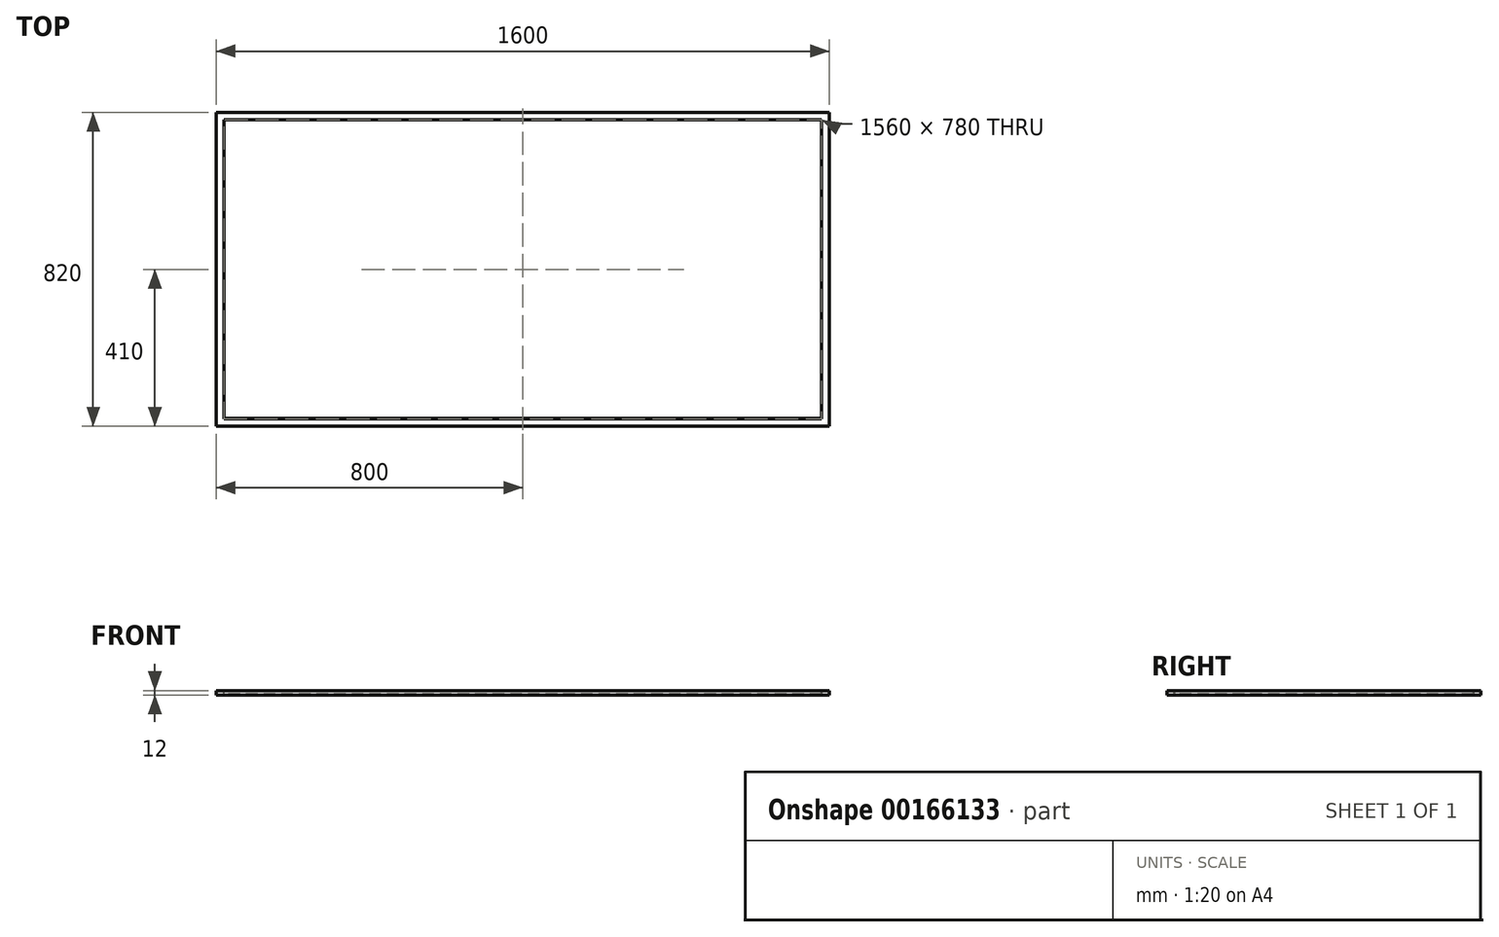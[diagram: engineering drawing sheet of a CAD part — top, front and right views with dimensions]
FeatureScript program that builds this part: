
annotation { "Feature Type Name" : "Feature", "Feature Type Description" : "" }
export const myFeature = defineFeature(function(context is Context, id is Id, definition is map)
    precondition{}
    {
        {
            var Q0;
            Q0=qCreatedBy(makeId("Front.planeOp"),FACE);
            var sketch = newSketch(context, id + "F0", { "sketchPlane" : qUnion([Q0])});
            skLineSegment(sketch, "E0.bottom", {"start": v(0, 0) * mm, "end": v(20, 0) * mm});
            skLineSegment(sketch, "E0.top", {"start": v(0, 12) * mm, "end": v(20, 12) * mm});
            skLineSegment(sketch, "E0.left", {"start": v(0, 0) * mm, "end": v(0, 12) * mm});
            skLineSegment(sketch, "E0.right", {"start": v(20, 0) * mm, "end": v(20, 12) * mm});
            skSolve(sketch);
        }
        {
            var Q0;
            Q0=qCreatedBy(makeId("Top.planeOp"),FACE);
            var sketch = newSketch(context, id + "F1", { "sketchPlane" : qUnion([Q0])});
            skLineSegment(sketch, "E1.bottom", {"start": v(0, 0) * mm, "end": v(1600, 0) * mm});
            skLineSegment(sketch, "E1.top", {"start": v(0, 820) * mm, "end": v(1600, 820) * mm});
            skLineSegment(sketch, "E1.left", {"start": v(0, 0) * mm, "end": v(0, 820) * mm});
            skLineSegment(sketch, "E1.right", {"start": v(1600, 0) * mm, "end": v(1600, 820) * mm});
            skSolve(sketch);
        }
        {
            var Q0;
            Q0=makeQuery(id+"F0.imprint","IMPRINT",FACE,{"disambiguationData":[TD([[makeQuery(id+"F0.imprint","IMPRINT",EDGE,{"derivedFrom":sQuery(id+"F0.wireOp",EDGE,"E0.bottom")}),1.0]])]});
            var Q1;
            Q1=sQuery(id+"F1.wireOp",EDGE,"E1.left");
            var Q2;
            Q2=sQuery(id+"F1.wireOp",EDGE,"E1.top");
            var Q3;
            Q3=sQuery(id+"F1.wireOp",EDGE,"E1.right");
            var Q4;
            Q4=sQuery(id+"F1.wireOp",EDGE,"E1.bottom");
            sweep(context, id + "F2", {"profiles" : qUnion([Q0]), "path" : qUnion([Q1, Q2, Q3, Q4])});
        }
        {
            var Q0;
            Q0=qCreatedBy(makeId("Top.planeOp"),FACE);
            cPlane(context, id + "F3", {"entities" : qUnion([Q0]), "cplaneType" : CPlaneType.OFFSET, "offset" : 6 * mm, "width" : 150 * mm, "height" : 150 * mm});
        }
        {
            var Q0;
            Q0=qCreatedBy(id+"F3.planeOp",FACE);
            var sketch = newSketch(context, id + "F4", { "sketchPlane" : qUnion([Q0])});
            skLineSegment(sketch, "E2.bottom", {"start": v(19.9, 20.6) * mm, "end": v(1579.9, 20.6) * mm});
            skLineSegment(sketch, "E2.top", {"start": v(19.9, 800.6) * mm, "end": v(1579.9, 800.6) * mm});
            skLineSegment(sketch, "E2.left", {"start": v(19.9, 20.6) * mm, "end": v(19.9, 800.6) * mm});
            skLineSegment(sketch, "E2.right", {"start": v(1579.9, 20.6) * mm, "end": v(1579.9, 800.6) * mm});
            skSolve(sketch);
        }
        {
            var Q0;
            Q0=makeQuery(id+"F4.imprint","IMPRINT",FACE,{"disambiguationData":[TD([[makeQuery(id+"F4.imprint","IMPRINT",EDGE,{"derivedFrom":sQuery(id+"F4.wireOp",EDGE,"E2.bottom")}),1.0]])]});
            extrude(context, id + "F5", {"entities" : qUnion([Q0]), "operationType" : NewBodyOperationType.ADD, "endBound" : BoundingType.SYMMETRIC, "depth" : 6 * mm});
        }
    });
